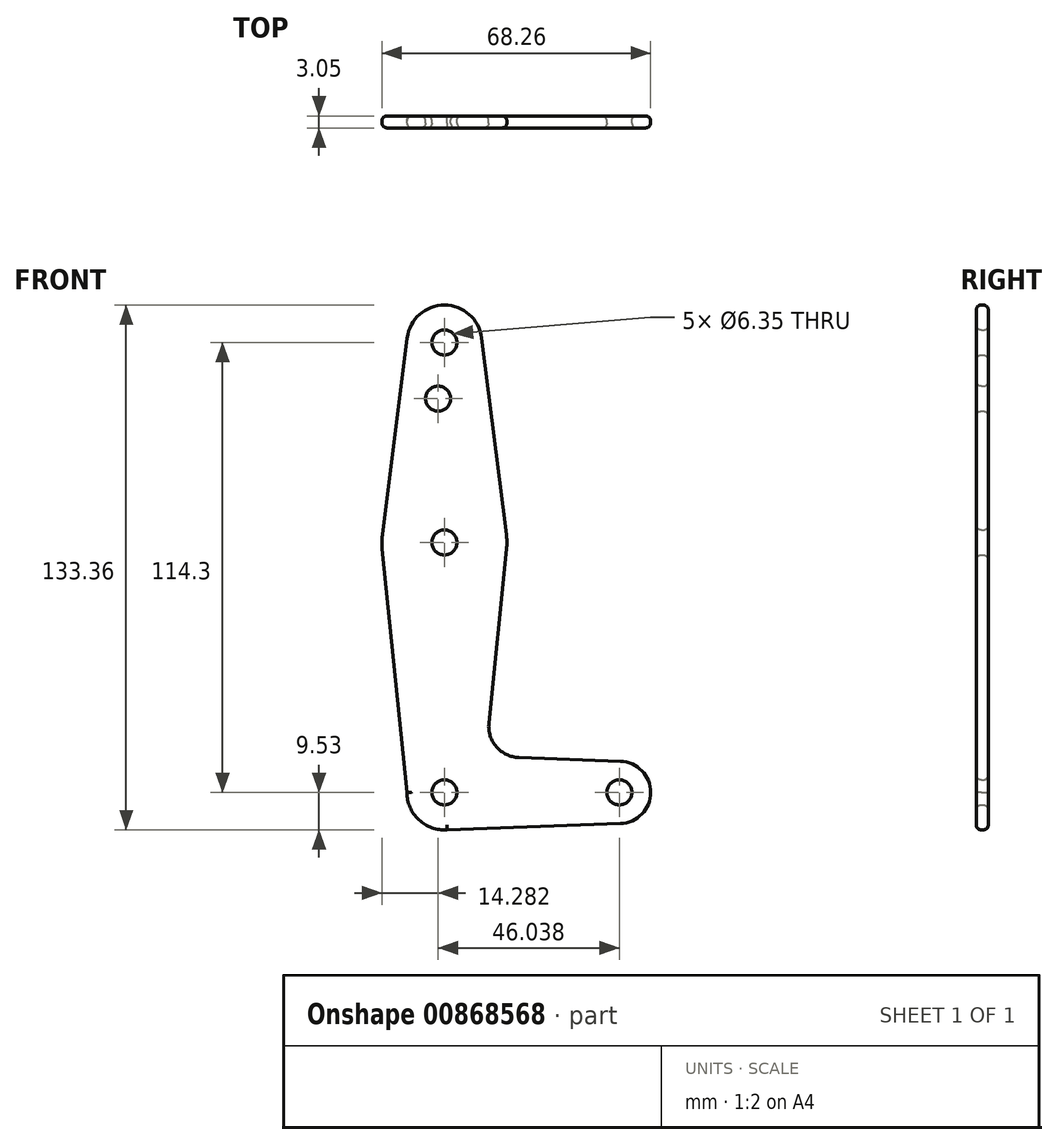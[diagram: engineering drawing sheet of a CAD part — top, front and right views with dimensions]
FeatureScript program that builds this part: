
annotation { "Feature Type Name" : "Feature", "Feature Type Description" : "" }
export const myFeature = defineFeature(function(context is Context, id is Id, definition is map)
    precondition{}
    {
        {
            var Q0;
            Q0=qCreatedBy(makeId("Front.planeOp"),FACE);
            var sketch = newSketch(context, id + "F0", { "sketchPlane" : qUnion([Q0])});
            skLineSegment(sketch, "E0", {"start": v(0, 114.3) * mm, "end": v(0, 0) * mm, "construction": true});
            skLineSegment(sketch, "E1", {"start": v(0, 0) * mm, "end": v(44.45, 0) * mm, "construction": true});
            skCircle(sketch, "E2", {"center": v(0, 114.3) * mm, "radius": 9.53 * mm});
            skCircle(sketch, "E3", {"center": v(0, 0) * mm, "radius": 9.53 * mm});
            skCircle(sketch, "E4", {"center": v(0, 63.5) * mm, "radius": 15.88 * mm});
            skCircle(sketch, "E5", {"center": v(44.45, 0) * mm, "radius": 7.94 * mm});
            skLineSegment(sketch, "E6", {"start": v(-9.45, 115.5) * mm, "end": v(-15.75, 65.48) * mm});
            skLineSegment(sketch, "E7", {"start": v(-9.53, 0) * mm, "end": v(-15.8, 61.9) * mm});
            skLineSegment(sketch, "E8", {"start": v(0, -9.53) * mm, "end": v(44.73, -7.93) * mm});
            skLineSegment(sketch, "E9", {"start": v(18.93, 8.85) * mm, "end": v(44.73, 7.93) * mm});
            skLineSegment(sketch, "E10", {"start": v(11.3, 17.6) * mm, "end": v(15.8, 61.9) * mm});
            skLineSegment(sketch, "E11", {"start": v(9.45, 115.5) * mm, "end": v(15.75, 65.48) * mm});
            skCircle(sketch, "E12", {"center": v(0, 114.3) * mm, "radius": 3.18 * mm});
            skCircle(sketch, "E13", {"center": v(0, 63.5) * mm, "radius": 3.18 * mm});
            skCircle(sketch, "E14", {"center": v(0, 0) * mm, "radius": 3.18 * mm});
            skCircle(sketch, "E15", {"center": v(44.45, 0) * mm, "radius": 3.18 * mm});
            skCircle(sketch, "E16", {"center": v(-1.59, 100.03) * mm, "radius": 3.18 * mm});
            skArc(sketch, "E17.filletArc", {"start": v(11.3, 17.6) * mm, "mid": v(13.22, 11.57) * mm, "end": v(18.93, 8.85) * mm});
            skSolve(sketch);
        }
        {
            var Q0;
            Q0 = qSketchRegion(id + "F0", true);
            extrude(context, id + "F1", {"entities" : qUnion([Q0]), "depth" : 3.05 * mm, "offsetDistance" : 25.4 * mm});
        }
        {
            var Q0;
            Q0=makeQuery(id+"F1.opExtrude","CAP_EDGE",EDGE,{"disambiguationData":[OSD([sQuery(id+"F0.wireOp",EDGE,"E12")])],"isStart":false});
            var Q1;
            Q1=makeQuery(id+"F1.opExtrude","CAP_EDGE",EDGE,{"disambiguationData":[OSD([sQuery(id+"F0.wireOp",EDGE,"E16")])],"isStart":false});
            var Q2;
            Q2=makeQuery(id+"F1.opExtrude","CAP_EDGE",EDGE,{"disambiguationData":[OSD([sQuery(id+"F0.wireOp",EDGE,"E12")])],"isStart":true});
            var Q3;
            Q3=makeQuery(id+"F1.opExtrude","CAP_EDGE",EDGE,{"disambiguationData":[OSD([sQuery(id+"F0.wireOp",EDGE,"E16")])],"isStart":true});
            var Q4;
            Q4=makeQuery(id+"F1.opExtrude","CAP_EDGE",EDGE,{"disambiguationData":[OSD([sQuery(id+"F0.wireOp",EDGE,"E13")])],"isStart":true});
            var Q5;
            Q5=makeQuery(id+"F1.opExtrude","CAP_EDGE",EDGE,{"disambiguationData":[OSD([sQuery(id+"F0.wireOp",EDGE,"E13")])],"isStart":false});
            var Q6;
            Q6=makeQuery(id+"F1.opExtrude","CAP_EDGE",EDGE,{"disambiguationData":[OSD([sQuery(id+"F0.wireOp",EDGE,"E14")])],"isStart":false});
            var Q7;
            Q7=makeQuery(id+"F1.opExtrude","CAP_EDGE",EDGE,{"disambiguationData":[OSD([sQuery(id+"F0.wireOp",EDGE,"E14")])],"isStart":true});
            var Q8;
            Q8=makeQuery(id+"F1.opExtrude","CAP_EDGE",EDGE,{"disambiguationData":[OSD([sQuery(id+"F0.wireOp",EDGE,"E15")])],"isStart":false});
            var Q9;
            Q9=makeQuery(id+"F1.opExtrude","CAP_EDGE",EDGE,{"disambiguationData":[OSD([sQuery(id+"F0.wireOp",EDGE,"E15")])],"isStart":true});
            var Q10;
            Q10=makeQuery(id+"F1.opExtrude","CAP_EDGE",EDGE,{"disambiguationData":[OSD([sQuery(id+"F0.wireOp",EDGE,"E11")])],"isStart":false});
            var Q11;
            Q11=makeQuery(id+"F1.opExtrude","CAP_EDGE",EDGE,{"disambiguationData":[OSD([sQuery(id+"F0.wireOp",EDGE,"E3")])],"isStart":false});
            var Q12;
            Q12=makeQuery(id+"F1.opExtrude","CAP_EDGE",EDGE,{"disambiguationData":[OSD([sQuery(id+"F0.wireOp",EDGE,"E8")])],"isStart":true});
            var Q13;
            Q13=makeQuery(id+"F1.opExtrude","CAP_EDGE",EDGE,{"disambiguationData":[OSD([sQuery(id+"F0.wireOp",EDGE,"E3")])],"isStart":true});
            fillet(context, id + "F2", {"entities" : qUnion([Q0, Q1, Q2, Q3, Q4, Q5, Q6, Q7, Q8, Q9, Q10, Q11, Q12, Q13]), "radius" : 1.27 * mm, "tangentPropagation" : true, "allowEdgeOverflow" : false});
        }
    });
